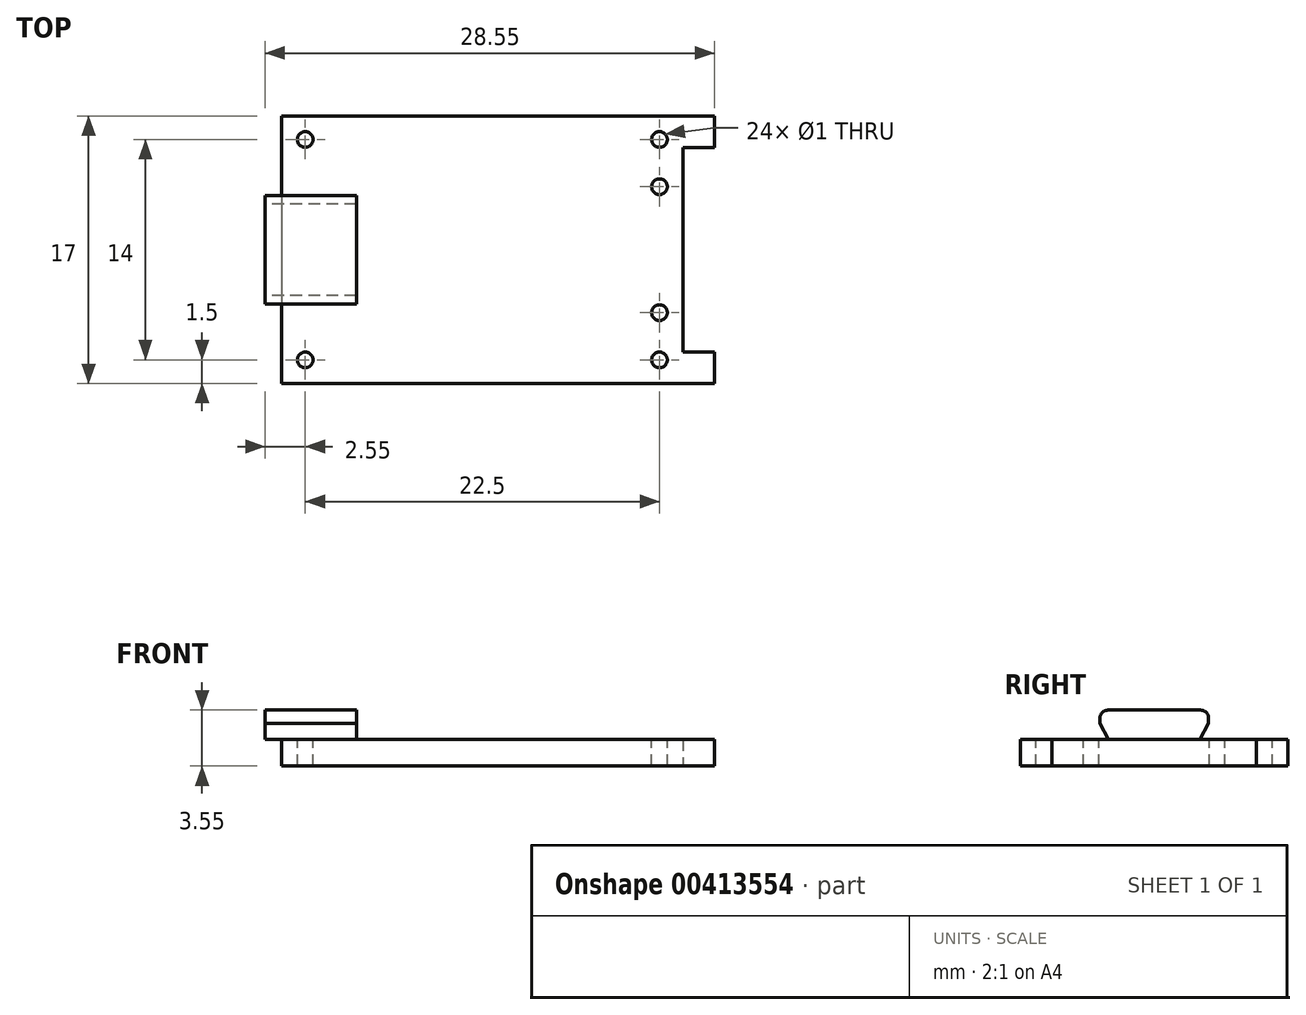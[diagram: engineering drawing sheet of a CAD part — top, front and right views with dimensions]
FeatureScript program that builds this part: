
annotation { "Feature Type Name" : "Feature", "Feature Type Description" : "" }
export const myFeature = defineFeature(function(context is Context, id is Id, definition is map)
    precondition{}
    {
        {
            var Q0;
            Q0=qCreatedBy(makeId("Top.planeOp"),FACE);
            var sketch = newSketch(context, id + "F0", { "sketchPlane" : qUnion([Q0])});
            skLineSegment(sketch, "E0.bottom", {"start": v(13.75, 8.5) * mm, "end": v(-13.75, 8.5) * mm});
            skLineSegment(sketch, "E0.top", {"start": v(13.75, -8.5) * mm, "end": v(-13.75, -8.5) * mm});
            skLineSegment(sketch, "E0.left", {"start": v(13.75, 8.5) * mm, "end": v(13.75, 6.5) * mm});
            skLineSegment(sketch, "E0.right", {"start": v(-13.75, 8.5) * mm, "end": v(-13.75, -8.5) * mm});
            skPoint(sketch, "E0.middle", {"position": v(0, 0) * mm});
            skLineSegment(sketch, "E1", {"start": v(13.75, 6.5) * mm, "end": v(11.75, 6.5) * mm});
            skLineSegment(sketch, "E2", {"start": v(11.75, 6.5) * mm, "end": v(11.75, -6.5) * mm});
            skLineSegment(sketch, "E3", {"start": v(11.75, -6.5) * mm, "end": v(13.75, -6.5) * mm});
            skLineSegment(sketch, "E4.trimOffspring", {"start": v(13.75, -6.5) * mm, "end": v(13.75, -8.5) * mm});
            skSolve(sketch);
        }
        {
            var Q0;
            Q0 = qSketchRegion(id + "F0", true);
            extrude(context, id + "F1", {"entities" : qUnion([Q0]), "depth" : 1.7 * mm});
        }
        {
            var Q0;
            Q0=makeQuery(id+"F1.opExtrude","CAP_FACE",FACE,{"disambiguationData":[OSD([sQuery(id+"F0.wireOp",EDGE,"E0.bottom"),sQuery(id+"F0.wireOp",EDGE,"E0.top"),sQuery(id+"F0.wireOp",EDGE,"E0.left"),sQuery(id+"F0.wireOp",EDGE,"E0.right"),sQuery(id+"F0.wireOp",EDGE,"E1"),sQuery(id+"F0.wireOp",EDGE,"E2"),sQuery(id+"F0.wireOp",EDGE,"E3"),sQuery(id+"F0.wireOp",EDGE,"E4.trimOffspring")])],"isStart":false});
            var sketch = newSketch(context, id + "F2", { "sketchPlane" : qUnion([Q0])});
            skCircle(sketch, "E5", {"center": v(10.25, 7) * mm, "radius": 0.5 * mm});
            skCircle(sketch, "E6", {"center": v(10.25, 4) * mm, "radius": 0.5 * mm});
            skCircle(sketch, "E7.MirrorC", {"center": v(10.25, -4) * mm, "radius": 0.5 * mm});
            skCircle(sketch, "E8.MirrorC", {"center": v(10.25, -7) * mm, "radius": 0.5 * mm});
            skCircle(sketch, "E9", {"center": v(-12.25, 7) * mm, "radius": 0.5 * mm});
            skCircle(sketch, "E10.MirrorC", {"center": v(-12.25, -7) * mm, "radius": 0.5 * mm});
            skSolve(sketch);
        }
        {
            var Q0;
            Q0 = qSketchRegion(id + "F2", true);
            extrude(context, id + "F3", {"entities" : qUnion([Q0]), "operationType" : NewBodyOperationType.REMOVE, "endBound" : BoundingType.THROUGH_ALL, "oppositeDirection" : true, "depth" : 25 * mm});
        }
        {
            var Q0;
            Q0=qCreatedBy(makeId("Right.planeOp"),FACE);
            cPlane(context, id + "F4", {"entities" : qUnion([Q0]), "cplaneType" : CPlaneType.OFFSET, "offset" : 13.8 * mm, "oppositeDirection" : true, "width" : 150 * mm, "height" : 150 * mm});
        }
        {
            var Q0;
            Q0=qCreatedBy(id+"F4.planeOp",FACE);
            var sketch = newSketch(context, id + "F5", { "sketchPlane" : qUnion([Q0])});
            skLineSegment(sketch, "E11.bottom", {"start": v(2.9, 1.7) * mm, "end": v(-2.9, 1.7) * mm});
            skLineSegment(sketch, "E11.top", {"start": v(2.95, 3.55) * mm, "end": v(-2.95, 3.55) * mm});
            skLineSegment(sketch, "E11.left", {"start": v(3.45, 2.7) * mm, "end": v(3.45, 3.05) * mm});
            skLineSegment(sketch, "E11.right", {"start": v(-3.45, 2.7) * mm, "end": v(-3.45, 3.05) * mm});
            skPoint(sketch, "E12.visualSharp", {"position": v(3.45, 3.55) * mm});
            skArc(sketch, "E12.filletArc", {"start": v(3.45, 3.05) * mm, "mid": v(3.3, 3.4) * mm, "end": v(2.95, 3.55) * mm});
            skPoint(sketch, "E13.visualSharp", {"position": v(-3.45, 3.55) * mm});
            skArc(sketch, "E13.filletArc", {"start": v(-2.95, 3.55) * mm, "mid": v(-3.3, 3.4) * mm, "end": v(-3.45, 3.05) * mm});
            skLineSegment(sketch, "E14", {"start": v(3.45, 2.7) * mm, "end": v(2.9, 1.7) * mm});
            skLineSegment(sketch, "E15", {"start": v(-3.45, 2.7) * mm, "end": v(-2.9, 1.7) * mm});
            skPoint(sketch, "E16.orphan", {"position": v(3.45, 1.7) * mm});
            skSolve(sketch);
        }
        {
            var Q0;
            Q0 = qSketchRegion(id + "F5", true);
            var Q1;
            Q1=sQuery(id+"F5.wireOp",EDGE,"E15");
            var Q2;
            Q2=sQuery(id+"F5.wireOp",EDGE,"E11.right");
            var Q3;
            Q3=sQuery(id+"F5.wireOp",EDGE,"E13.filletArc");
            var Q4;
            Q4=sQuery(id+"F5.wireOp",EDGE,"E11.top");
            var Q5;
            Q5=sQuery(id+"F5.wireOp",EDGE,"E12.filletArc");
            var Q6;
            Q6=sQuery(id+"F5.wireOp",EDGE,"E11.left");
            var Q7;
            Q7=sQuery(id+"F5.wireOp",EDGE,"E14");
            var Q8;
            Q8=sQuery(id+"F5.wireOp",EDGE,"E11.bottom");
            extrude(context, id + "F6", {"entities" : qUnion([Q0]), "surfaceEntities" : qUnion([Q1, Q2, Q3, Q4, Q5, Q6, Q7, Q8]), "depth" : 4.8 * mm, "hasSecondDirection" : true, "secondDirectionOppositeDirection" : true, "secondDirectionDepth" : 1 * mm});
        }
    });
